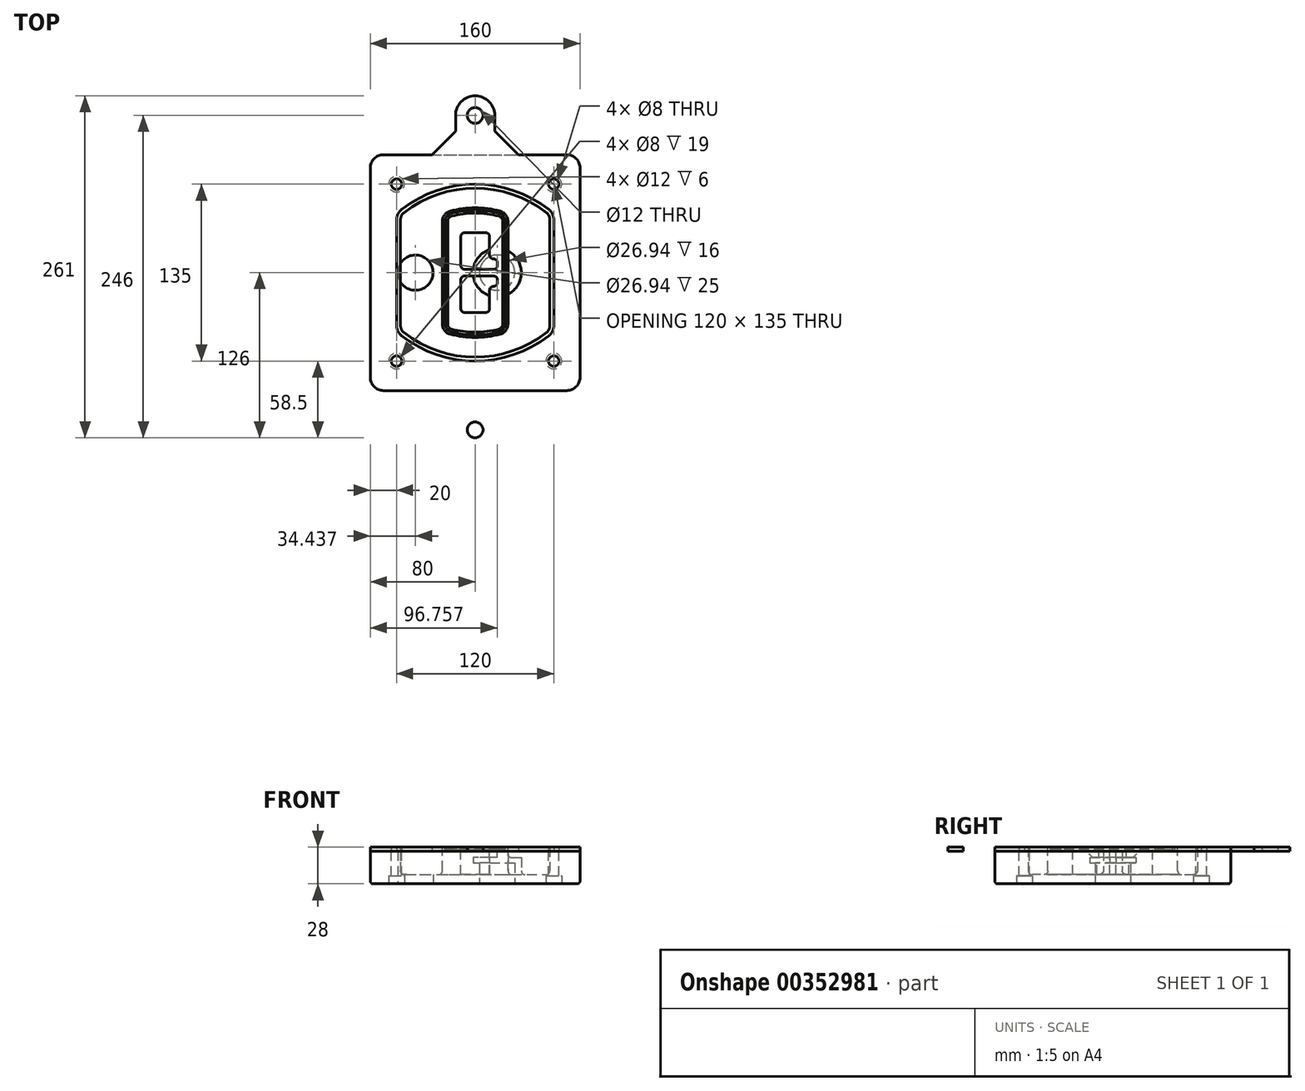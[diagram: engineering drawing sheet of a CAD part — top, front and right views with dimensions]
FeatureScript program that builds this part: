
annotation { "Feature Type Name" : "Feature", "Feature Type Description" : "" }
export const myFeature = defineFeature(function(context is Context, id is Id, definition is map)
    precondition{}
    {
        {
            var Q0;
            Q0=qCreatedBy(makeId("Top.planeOp"),FACE);
            var sketch = newSketch(context, id + "F0", { "sketchPlane" : qUnion([Q0])});
            skPoint(sketch, "E0.rect.middle", {"position": v(0, 0) * mm});
            skLineSegment(sketch, "E1.bottom", {"start": v(-70, -90) * mm, "end": v(70, -90) * mm});
            skLineSegment(sketch, "E1.top", {"start": v(-70, 90) * mm, "end": v(70, 90) * mm});
            skLineSegment(sketch, "E1.left", {"start": v(-80, -80) * mm, "end": v(-80, 80) * mm});
            skLineSegment(sketch, "E1.right", {"start": v(80, -80) * mm, "end": v(80, 80) * mm});
            skLineSegment(sketch, "E2", {"start": v(-80, 90) * mm, "end": v(80, -90) * mm, "construction": true});
            skLineSegment(sketch, "E3", {"start": v(80, 90) * mm, "end": v(-80, -90) * mm, "construction": true});
            skCircle(sketch, "E4", {"center": v(-60, 67.5) * mm, "radius": 4 * mm});
            skCircle(sketch, "E5", {"center": v(60, 67.5) * mm, "radius": 4 * mm});
            skCircle(sketch, "E6", {"center": v(60, -67.5) * mm, "radius": 4 * mm});
            skCircle(sketch, "E7", {"center": v(-60, -67.5) * mm, "radius": 4 * mm});
            skLineSegment(sketch, "E8", {"start": v(-60, 67.5) * mm, "end": v(60, 67.5) * mm, "construction": true});
            skLineSegment(sketch, "E9", {"start": v(60, 67.5) * mm, "end": v(60, -67.5) * mm, "construction": true});
            skLineSegment(sketch, "E10", {"start": v(60, -67.5) * mm, "end": v(-60, -67.5) * mm, "construction": true});
            skLineSegment(sketch, "E11", {"start": v(-60, -67.5) * mm, "end": v(-60, 67.5) * mm, "construction": true});
            skLineSegment(sketch, "E12", {"start": v(-60, 40.3) * mm, "end": v(-60, -40.3) * mm});
            skLineSegment(sketch, "E13", {"start": v(60, 40.3) * mm, "end": v(60, -40.3) * mm});
            skArc(sketch, "E14", {"start": v(56.15, 48.18) * mm, "mid": v(0, 67.5) * mm, "end": v(-56.15, 48.18) * mm});
            skArc(sketch, "E15", {"start": v(-56.15, -48.18) * mm, "mid": v(0, -67.5) * mm, "end": v(56.15, -48.18) * mm});
            skLineSegment(sketch, "E16", {"start": v(-60, 0) * mm, "end": v(60, 0) * mm, "construction": true});
            skPoint(sketch, "E17.visualSharp", {"position": v(-60, -45) * mm});
            skArc(sketch, "E17.filletArc", {"start": v(-60, -40.3) * mm, "mid": v(-58.99, -44.68) * mm, "end": v(-56.15, -48.18) * mm});
            skPoint(sketch, "E18.visualSharp", {"position": v(-60, 45) * mm});
            skArc(sketch, "E18.filletArc", {"start": v(-56.15, 48.18) * mm, "mid": v(-58.99, 44.68) * mm, "end": v(-60, 40.3) * mm});
            skPoint(sketch, "E19.visualSharp", {"position": v(60, 45) * mm});
            skArc(sketch, "E19.filletArc", {"start": v(60, 40.3) * mm, "mid": v(58.99, 44.68) * mm, "end": v(56.15, 48.18) * mm});
            skPoint(sketch, "E20.visualSharp", {"position": v(60, -45) * mm});
            skArc(sketch, "E20.filletArc", {"start": v(56.15, -48.18) * mm, "mid": v(58.99, -44.68) * mm, "end": v(60, -40.3) * mm});
            skPoint(sketch, "E21.visualSharp", {"position": v(-80, 90) * mm});
            skArc(sketch, "E21.filletArc", {"start": v(-70, 90) * mm, "mid": v(-77.07, 87.07) * mm, "end": v(-80, 80) * mm});
            skPoint(sketch, "E22.visualSharp", {"position": v(80, 90) * mm});
            skArc(sketch, "E22.filletArc", {"start": v(80, 80) * mm, "mid": v(77.07, 87.07) * mm, "end": v(70, 90) * mm});
            skPoint(sketch, "E23.visualSharp", {"position": v(80, -90) * mm});
            skArc(sketch, "E23.filletArc", {"start": v(70, -90) * mm, "mid": v(77.07, -87.07) * mm, "end": v(80, -80) * mm});
            skPoint(sketch, "E24.visualSharp", {"position": v(-80, -90) * mm});
            skArc(sketch, "E24.filletArc", {"start": v(-80, -80) * mm, "mid": v(-77.07, -87.07) * mm, "end": v(-70, -90) * mm});
            skArc(sketch, "E25.0", {"start": v(57, 40.3) * mm, "mid": v(56.3, 43.36) * mm, "end": v(54.3, 45.81) * mm});
            skLineSegment(sketch, "E25.1", {"start": v(57, 40.3) * mm, "end": v(57, -40.3) * mm});
            skArc(sketch, "E25.2", {"start": v(54.3, -45.81) * mm, "mid": v(56.3, -43.36) * mm, "end": v(57, -40.3) * mm});
            skArc(sketch, "E25.3", {"start": v(-54.3, -45.81) * mm, "mid": v(0, -64.5) * mm, "end": v(54.3, -45.81) * mm});
            skArc(sketch, "E25.4", {"start": v(-57, -40.3) * mm, "mid": v(-56.3, -43.36) * mm, "end": v(-54.3, -45.81) * mm});
            skArc(sketch, "E25.5", {"start": v(54.3, 45.81) * mm, "mid": v(0, 64.5) * mm, "end": v(-54.3, 45.81) * mm});
            skLineSegment(sketch, "E25.6", {"start": v(-57, 40.3) * mm, "end": v(-57, -40.3) * mm});
            skArc(sketch, "E25.7", {"start": v(-54.3, 45.81) * mm, "mid": v(-56.3, 43.36) * mm, "end": v(-57, 40.3) * mm});
            skArc(sketch, "E26.0", {"start": v(-58.62, 51.33) * mm, "mid": v(-62.58, 46.43) * mm, "end": v(-64, 40.3) * mm});
            skArc(sketch, "E26.1", {"start": v(58.62, 51.33) * mm, "mid": v(0, 71.5) * mm, "end": v(-58.62, 51.33) * mm});
            skArc(sketch, "E26.2", {"start": v(64, 40.3) * mm, "mid": v(62.58, 46.43) * mm, "end": v(58.62, 51.33) * mm});
            skLineSegment(sketch, "E26.3", {"start": v(64, 40.3) * mm, "end": v(64, -40.3) * mm});
            skArc(sketch, "E26.4", {"start": v(58.62, -51.33) * mm, "mid": v(62.58, -46.43) * mm, "end": v(64, -40.3) * mm});
            skLineSegment(sketch, "E26.5", {"start": v(-64, 40.3) * mm, "end": v(-64, -40.3) * mm});
            skArc(sketch, "E26.6", {"start": v(-58.62, -51.33) * mm, "mid": v(0, -71.5) * mm, "end": v(58.62, -51.33) * mm});
            skArc(sketch, "E26.7", {"start": v(-64, -40.3) * mm, "mid": v(-62.58, -46.43) * mm, "end": v(-58.62, -51.33) * mm});
            skSolve(sketch);
        }
        {
            var Q0;
            Q0=makeQuery(id+"F0.imprint","IMPRINT",FACE,{"disambiguationData":[TD([[makeQuery(id+"F0.imprint","IMPRINT",EDGE,{"derivedFrom":sQuery(id+"F0.wireOp",EDGE,"E1.bottom")}),1.0]])]});
            var Q1;
            Q1=makeQuery(id+"F0.imprint","IMPRINT",FACE,{"disambiguationData":[TD([[makeQuery(id+"F0.imprint","IMPRINT",EDGE,{"derivedFrom":sQuery(id+"F0.wireOp",EDGE,"E12")}),1.0]])]});
            var Q2;
            Q2=makeQuery(id+"F0.imprint","IMPRINT",FACE,{"disambiguationData":[TD([[makeQuery(id+"F0.imprint","IMPRINT",EDGE,{"derivedFrom":sQuery(id+"F0.wireOp",EDGE,"E25.0")}),1.0]])]});
            var Q3;
            Q3=makeQuery(id+"F0.imprint","IMPRINT",FACE,{"disambiguationData":[TD([[makeQuery(id+"F0.imprint","IMPRINT",EDGE,{"derivedFrom":sQuery(id+"F0.wireOp",EDGE,"E12")}),-1.0]])]});
            extrude(context, id + "F1", {"entities" : qUnion([Q0, Q1, Q2, Q3]), "oppositeDirection" : true, "depth" : 25 * mm});
        }
        {
            var Q0;
            Q0=makeQuery(id+"F0.imprint","IMPRINT",FACE,{"disambiguationData":[TD([[makeQuery(id+"F0.imprint","IMPRINT",EDGE,{"derivedFrom":sQuery(id+"F0.wireOp",EDGE,"E12")}),1.0]])]});
            extrude(context, id + "F2", {"entities" : qUnion([Q0]), "operationType" : NewBodyOperationType.ADD, "depth" : 3 * mm});
        }
        {
            var Q0;
            Q0=makeQuery(id+"F0.imprint","IMPRINT",FACE,{"disambiguationData":[TD([[makeQuery(id+"F0.imprint","IMPRINT",EDGE,{"derivedFrom":sQuery(id+"F0.wireOp",EDGE,"E25.0")}),1.0]])]});
            extrude(context, id + "F3", {"entities" : qUnion([Q0]), "operationType" : NewBodyOperationType.REMOVE, "oppositeDirection" : true, "depth" : 18 * mm});
        }
        {
            var Q0;
            Q0=makeQuery(id+"F2.opExtrude","CAP_FACE",FACE,{"disambiguationData":[OSD([sQuery(id+"F0.wireOp",EDGE,"E12"),sQuery(id+"F0.wireOp",EDGE,"E13"),sQuery(id+"F0.wireOp",EDGE,"E14"),sQuery(id+"F0.wireOp",EDGE,"E15"),sQuery(id+"F0.wireOp",EDGE,"E17.filletArc"),sQuery(id+"F0.wireOp",EDGE,"E18.filletArc"),sQuery(id+"F0.wireOp",EDGE,"E19.filletArc"),sQuery(id+"F0.wireOp",EDGE,"E20.filletArc"),sQuery(id+"F0.wireOp",EDGE,"E25.0"),sQuery(id+"F0.wireOp",EDGE,"E25.1"),sQuery(id+"F0.wireOp",EDGE,"E25.2"),sQuery(id+"F0.wireOp",EDGE,"E25.3"),sQuery(id+"F0.wireOp",EDGE,"E25.4"),sQuery(id+"F0.wireOp",EDGE,"E25.5"),sQuery(id+"F0.wireOp",EDGE,"E25.6"),sQuery(id+"F0.wireOp",EDGE,"E25.7")])],"isStart":false});
            var sketch = newSketch(context, id + "F4", { "sketchPlane" : qUnion([Q0])});
            skArc(sketch, "E27.0", {"start": v(-19.08, -46.97) * mm, "mid": v(0, -49.5) * mm, "end": v(19.08, -46.97) * mm});
            skArc(sketch, "E28.0", {"start": v(19.08, 46.97) * mm, "mid": v(0, 49.5) * mm, "end": v(-19.08, 46.97) * mm});
            skLineSegment(sketch, "E29", {"start": v(-25, 39.25) * mm, "end": v(-25, -39.25) * mm});
            skLineSegment(sketch, "E30", {"start": v(25, 39.25) * mm, "end": v(25, -39.25) * mm});
            skLineSegment(sketch, "E31", {"start": v(-25, 45.1) * mm, "end": v(25, 45.1) * mm, "construction": true});
            skLineSegment(sketch, "E32", {"start": v(-25, -45.1) * mm, "end": v(25, -45.1) * mm, "construction": true});
            skPoint(sketch, "E33.visualSharp", {"position": v(-25, 45.1) * mm});
            skArc(sketch, "E33.filletArc", {"start": v(-19.08, 46.97) * mm, "mid": v(-23.35, 44.11) * mm, "end": v(-25, 39.25) * mm});
            skPoint(sketch, "E34.visualSharp", {"position": v(25, 45.1) * mm});
            skArc(sketch, "E34.filletArc", {"start": v(25, 39.25) * mm, "mid": v(23.35, 44.11) * mm, "end": v(19.08, 46.97) * mm});
            skPoint(sketch, "E35.visualSharp", {"position": v(25, -45.1) * mm});
            skArc(sketch, "E35.filletArc", {"start": v(19.08, -46.97) * mm, "mid": v(23.35, -44.11) * mm, "end": v(25, -39.25) * mm});
            skPoint(sketch, "E36.visualSharp", {"position": v(-25, -45.1) * mm});
            skArc(sketch, "E36.filletArc", {"start": v(-25, -39.25) * mm, "mid": v(-23.35, -44.11) * mm, "end": v(-19.08, -46.97) * mm});
            skArc(sketch, "E37.0", {"start": v(54.3, 45.81) * mm, "mid": v(0, 64.5) * mm, "end": v(-54.3, 45.81) * mm});
            skArc(sketch, "E37.1", {"start": v(-54.3, 45.81) * mm, "mid": v(-56.3, 43.36) * mm, "end": v(-57, 40.3) * mm});
            skLineSegment(sketch, "E37.2", {"start": v(-57, 40.3) * mm, "end": v(-57, -40.3) * mm});
            skArc(sketch, "E37.3", {"start": v(-57, -40.3) * mm, "mid": v(-56.3, -43.36) * mm, "end": v(-54.3, -45.81) * mm});
            skArc(sketch, "E37.4", {"start": v(-54.3, -45.81) * mm, "mid": v(0, -64.5) * mm, "end": v(54.3, -45.81) * mm});
            skArc(sketch, "E37.5", {"start": v(54.3, -45.81) * mm, "mid": v(56.3, -43.36) * mm, "end": v(57, -40.3) * mm});
            skLineSegment(sketch, "E37.6", {"start": v(57, 40.3) * mm, "end": v(57, -40.3) * mm});
            skArc(sketch, "E37.7", {"start": v(57, 40.3) * mm, "mid": v(56.3, 43.36) * mm, "end": v(54.3, 45.81) * mm});
            skLineSegment(sketch, "E38.0", {"start": v(23, 39.25) * mm, "end": v(23, -39.25) * mm});
            skArc(sketch, "E38.1", {"start": v(18.56, -45.04) * mm, "mid": v(21.76, -42.9) * mm, "end": v(23, -39.25) * mm});
            skArc(sketch, "E38.2", {"start": v(-18.56, -45.04) * mm, "mid": v(0, -47.5) * mm, "end": v(18.56, -45.04) * mm});
            skArc(sketch, "E38.3", {"start": v(-23, -39.25) * mm, "mid": v(-21.76, -42.9) * mm, "end": v(-18.56, -45.04) * mm});
            skLineSegment(sketch, "E38.4", {"start": v(-23, 39.25) * mm, "end": v(-23, -39.25) * mm});
            skArc(sketch, "E38.5", {"start": v(23, 39.25) * mm, "mid": v(21.76, 42.9) * mm, "end": v(18.56, 45.04) * mm});
            skArc(sketch, "E38.6", {"start": v(-18.56, 45.04) * mm, "mid": v(-21.76, 42.9) * mm, "end": v(-23, 39.25) * mm});
            skArc(sketch, "E38.7", {"start": v(18.56, 45.04) * mm, "mid": v(0, 47.5) * mm, "end": v(-18.56, 45.04) * mm});
            skArc(sketch, "E39.0", {"start": v(21, 39.25) * mm, "mid": v(20.18, 41.68) * mm, "end": v(18.04, 43.1) * mm});
            skLineSegment(sketch, "E39.1", {"start": v(21, 39.25) * mm, "end": v(21, -39.25) * mm});
            skArc(sketch, "E39.2", {"start": v(18.04, -43.1) * mm, "mid": v(20.18, -41.68) * mm, "end": v(21, -39.25) * mm});
            skArc(sketch, "E39.3", {"start": v(-18.04, -43.1) * mm, "mid": v(0, -45.5) * mm, "end": v(18.04, -43.1) * mm});
            skArc(sketch, "E39.4", {"start": v(-21, -39.25) * mm, "mid": v(-20.18, -41.68) * mm, "end": v(-18.04, -43.1) * mm});
            skArc(sketch, "E39.5", {"start": v(18.04, 43.1) * mm, "mid": v(0, 45.5) * mm, "end": v(-18.04, 43.1) * mm});
            skLineSegment(sketch, "E39.6", {"start": v(-21, 39.25) * mm, "end": v(-21, -39.25) * mm});
            skArc(sketch, "E39.7", {"start": v(-18.04, 43.1) * mm, "mid": v(-20.18, 41.68) * mm, "end": v(-21, 39.25) * mm});
            skLineSegment(sketch, "E40", {"start": v(-25, 0) * mm, "end": v(25, 0) * mm, "construction": true});
            skLineSegment(sketch, "E41", {"start": v(-11, 5.5) * mm, "end": v(-11, 27.5) * mm});
            skLineSegment(sketch, "E42", {"start": v(-8, 30.5) * mm, "end": v(8, 30.5) * mm});
            skLineSegment(sketch, "E43", {"start": v(11, 27.5) * mm, "end": v(11, 13.5) * mm});
            skLineSegment(sketch, "E44", {"start": v(14, 10.5) * mm, "end": v(14, 10.5) * mm});
            skLineSegment(sketch, "E45", {"start": v(17, 7.5) * mm, "end": v(17, 5.5) * mm});
            skLineSegment(sketch, "E46", {"start": v(14, 2.5) * mm, "end": v(-8, 2.5) * mm});
            skPoint(sketch, "E47.visualSharp", {"position": v(-11, 30.5) * mm});
            skArc(sketch, "E47.filletArc", {"start": v(-8, 30.5) * mm, "mid": v(-10.12, 29.62) * mm, "end": v(-11, 27.5) * mm});
            skPoint(sketch, "E48.visualSharp", {"position": v(11, 30.5) * mm});
            skArc(sketch, "E48.filletArc", {"start": v(11, 27.5) * mm, "mid": v(10.12, 29.62) * mm, "end": v(8, 30.5) * mm});
            skPoint(sketch, "E49.visualSharp", {"position": v(11, 10.5) * mm});
            skArc(sketch, "E49.filletArc", {"start": v(11, 13.5) * mm, "mid": v(11.88, 11.38) * mm, "end": v(14, 10.5) * mm});
            skPoint(sketch, "E50.visualSharp", {"position": v(17, 10.5) * mm});
            skArc(sketch, "E50.filletArc", {"start": v(17, 7.5) * mm, "mid": v(16.12, 9.62) * mm, "end": v(14, 10.5) * mm});
            skPoint(sketch, "E51.visualSharp", {"position": v(17, 2.5) * mm});
            skArc(sketch, "E51.filletArc", {"start": v(14, 2.5) * mm, "mid": v(16.12, 3.38) * mm, "end": v(17, 5.5) * mm});
            skPoint(sketch, "E52.visualSharp", {"position": v(-11, 2.5) * mm});
            skArc(sketch, "E52.filletArc", {"start": v(-11, 5.5) * mm, "mid": v(-10.12, 3.38) * mm, "end": v(-8, 2.5) * mm});
            skLineSegment(sketch, "E53.0.MirrorCS", {"start": v(14, -2.5) * mm, "end": v(-8, -2.5) * mm});
            skArc(sketch, "E54.0.MirrorCS", {"start": v(-11, -5.5) * mm, "mid": v(-10.12, -3.38) * mm, "end": v(-8, -2.5) * mm});
            skLineSegment(sketch, "E55.0.MirrorCS", {"start": v(-11, -5.5) * mm, "end": v(-11, -27.5) * mm});
            skArc(sketch, "E56.0.MirrorCS", {"start": v(-8, -30.5) * mm, "mid": v(-10.12, -29.62) * mm, "end": v(-11, -27.5) * mm});
            skLineSegment(sketch, "E57.0.MirrorCS", {"start": v(-8, -30.5) * mm, "end": v(8, -30.5) * mm});
            skArc(sketch, "E58.0.MirrorCS", {"start": v(11, -27.5) * mm, "mid": v(10.12, -29.62) * mm, "end": v(8, -30.5) * mm});
            skLineSegment(sketch, "E59.0.MirrorCS", {"start": v(11, -27.5) * mm, "end": v(11, -13.5) * mm});
            skArc(sketch, "E60.0.MirrorCS", {"start": v(11, -13.5) * mm, "mid": v(11.88, -11.38) * mm, "end": v(14, -10.5) * mm});
            skArc(sketch, "E61.0.MirrorCS", {"start": v(17, -7.5) * mm, "mid": v(16.12, -9.62) * mm, "end": v(14, -10.5) * mm});
            skLineSegment(sketch, "E62.0.MirrorCS", {"start": v(17, -7.5) * mm, "end": v(17, -5.5) * mm});
            skArc(sketch, "E63.0.MirrorCS", {"start": v(14, -2.5) * mm, "mid": v(16.12, -3.38) * mm, "end": v(17, -5.5) * mm});
            skSolve(sketch);
        }
        {
            var Q0;
            Q0=makeQuery(id+"F4.imprint","IMPRINT",FACE,{"disambiguationData":[TD([[makeQuery(id+"F4.imprint","IMPRINT",EDGE,{"derivedFrom":sQuery(id+"F4.wireOp",EDGE,"E27.0")}),1.0]])]});
            var Q1;
            Q1=makeQuery(id+"F4.imprint","IMPRINT",FACE,{"disambiguationData":[TD([[makeQuery(id+"F4.imprint","IMPRINT",EDGE,{"derivedFrom":sQuery(id+"F4.wireOp",EDGE,"E38.0")}),-1.0]])]});
            var Q2;
            Q2=makeQuery(id+"F4.imprint","IMPRINT",FACE,{"disambiguationData":[TD([[makeQuery(id+"F4.imprint","IMPRINT",EDGE,{"derivedFrom":sQuery(id+"F4.wireOp",EDGE,"E39.0")}),1.0]])]});
            extrude(context, id + "F5", {"entities" : qUnion([Q0, Q1, Q2]), "operationType" : NewBodyOperationType.ADD, "endBound" : BoundingType.UP_TO_NEXT, "oppositeDirection" : true, "depth" : 25 * mm});
        }
        {
            var Q0;
            Q0=makeQuery(id+"F4.imprint","IMPRINT",FACE,{"disambiguationData":[TD([[makeQuery(id+"F4.imprint","IMPRINT",EDGE,{"derivedFrom":sQuery(id+"F4.wireOp",EDGE,"E38.0")}),-1.0]])]});
            extrude(context, id + "F6", {"entities" : qUnion([Q0]), "operationType" : NewBodyOperationType.REMOVE, "oppositeDirection" : true, "depth" : 2 * mm});
        }
        {
            var Q0;
            Q0=makeQuery(id+"F1.opExtrude","CAP_FACE",FACE,{"disambiguationData":[OSD([sQuery(id+"F0.wireOp",EDGE,"E1.bottom"),sQuery(id+"F0.wireOp",EDGE,"E1.top"),sQuery(id+"F0.wireOp",EDGE,"E1.left"),sQuery(id+"F0.wireOp",EDGE,"E1.right"),sQuery(id+"F0.wireOp",EDGE,"E4"),sQuery(id+"F0.wireOp",EDGE,"E5"),sQuery(id+"F0.wireOp",EDGE,"E6"),sQuery(id+"F0.wireOp",EDGE,"E7"),sQuery(id+"F0.wireOp",EDGE,"E21.filletArc"),sQuery(id+"F0.wireOp",EDGE,"E22.filletArc"),sQuery(id+"F0.wireOp",EDGE,"E23.filletArc"),sQuery(id+"F0.wireOp",EDGE,"E24.filletArc")])],"isStart":false});
            var sketch = newSketch(context, id + "F7", { "sketchPlane" : qUnion([Q0])});
            skCircle(sketch, "E64", {"center": v(16.76, 0) * mm, "radius": 13.47 * mm});
            skCircle(sketch, "E65", {"center": v(-45.56, 0) * mm, "radius": 13.47 * mm});
            skLineSegment(sketch, "E66", {"start": v(80, 0) * mm, "end": v(-80, 0) * mm});
            skCircle(sketch, "E67", {"center": v(16.76, 0) * mm, "radius": 18.47 * mm});
            skCircle(sketch, "E68", {"center": v(60, -67.5) * mm, "radius": 6 * mm});
            skCircle(sketch, "E69", {"center": v(-60, -67.5) * mm, "radius": 6 * mm});
            skCircle(sketch, "E70", {"center": v(-60, 67.5) * mm, "radius": 6 * mm});
            skCircle(sketch, "E71", {"center": v(60, 67.5) * mm, "radius": 6 * mm});
            skSolve(sketch);
        }
        {
            var Q0;
            {var subQ1=sQuery(id+"F7.wireOp",EDGE,"E66");var subQ4=sQuery(id+"F7.wireOp",EDGE,"E64");var subQ6=makeQuery(id+"F7.imprint","INTERSECT",VERTEX,{"disambiguationData":[OD(0.0)],"derivedFrom":[subQ4,subQ1]});Q0=makeQuery(id+"F7.imprint","IMPRINT",FACE,{"disambiguationData":[TD([[makeQuery(id+"F7.imprint","IMPRINT",EDGE,{"disambiguationData":[TD([[subQ6,-1.0]])],"derivedFrom":subQ4}),-1.0]])]});}
            var Q1;
            {var subQ0=sQuery(id+"F7.wireOp",EDGE,"E66");var subQ1=sQuery(id+"F7.wireOp",EDGE,"E64");var subQ3=makeQuery(id+"F7.imprint","INTERSECT",VERTEX,{"disambiguationData":[OD(0.0)],"derivedFrom":[subQ1,subQ0]});Q1=makeQuery(id+"F7.imprint","IMPRINT",FACE,{"disambiguationData":[TD([[makeQuery(id+"F7.imprint","IMPRINT",EDGE,{"disambiguationData":[TD([[subQ3,-1.0]])],"derivedFrom":subQ1}),1.0]])]});}
            var Q2;
            {var subQ0=sQuery(id+"F7.wireOp",EDGE,"E66");var subQ1=sQuery(id+"F7.wireOp",EDGE,"E64");var subQ3=makeQuery(id+"F7.imprint","INTERSECT",VERTEX,{"disambiguationData":[OD(0.0)],"derivedFrom":[subQ1,subQ0]});Q2=makeQuery(id+"F7.imprint","IMPRINT",FACE,{"disambiguationData":[TD([[makeQuery(id+"F7.imprint","IMPRINT",EDGE,{"disambiguationData":[TD([[subQ3,1.0]])],"derivedFrom":subQ1}),1.0]])]});}
            var Q3;
            {var subQ1=sQuery(id+"F7.wireOp",EDGE,"E66");var subQ4=sQuery(id+"F7.wireOp",EDGE,"E64");var subQ6=makeQuery(id+"F7.imprint","INTERSECT",VERTEX,{"disambiguationData":[OD(0.0)],"derivedFrom":[subQ4,subQ1]});Q3=makeQuery(id+"F7.imprint","IMPRINT",FACE,{"disambiguationData":[TD([[makeQuery(id+"F7.imprint","IMPRINT",EDGE,{"disambiguationData":[TD([[subQ6,1.0]])],"derivedFrom":subQ4}),-1.0]])]});}
            extrude(context, id + "F8", {"entities" : qUnion([Q0, Q1, Q2, Q3]), "operationType" : NewBodyOperationType.ADD, "oppositeDirection" : true, "depth" : 20 * mm});
        }
        {
            var Q0;
            {var subQ0=sQuery(id+"F7.wireOp",EDGE,"E66");var subQ1=sQuery(id+"F7.wireOp",EDGE,"E64");var subQ3=makeQuery(id+"F7.imprint","INTERSECT",VERTEX,{"disambiguationData":[OD(0.0)],"derivedFrom":[subQ1,subQ0]});Q0=makeQuery(id+"F7.imprint","IMPRINT",FACE,{"disambiguationData":[TD([[makeQuery(id+"F7.imprint","IMPRINT",EDGE,{"disambiguationData":[TD([[subQ3,-1.0]])],"derivedFrom":subQ1}),1.0]])]});}
            var Q1;
            {var subQ0=sQuery(id+"F7.wireOp",EDGE,"E66");var subQ1=sQuery(id+"F7.wireOp",EDGE,"E64");var subQ3=makeQuery(id+"F7.imprint","INTERSECT",VERTEX,{"disambiguationData":[OD(0.0)],"derivedFrom":[subQ1,subQ0]});Q1=makeQuery(id+"F7.imprint","IMPRINT",FACE,{"disambiguationData":[TD([[makeQuery(id+"F7.imprint","IMPRINT",EDGE,{"disambiguationData":[TD([[subQ3,1.0]])],"derivedFrom":subQ1}),1.0]])]});}
            extrude(context, id + "F9", {"entities" : qUnion([Q0, Q1]), "operationType" : NewBodyOperationType.REMOVE, "oppositeDirection" : true, "depth" : 16 * mm});
        }
        {
            var Q0;
            {var subQ0=sQuery(id+"F7.wireOp",EDGE,"E66");var subQ1=sQuery(id+"F7.wireOp",EDGE,"E65");var subQ3=makeQuery(id+"F7.imprint","INTERSECT",VERTEX,{"disambiguationData":[OD(0.0)],"derivedFrom":[subQ1,subQ0]});Q0=makeQuery(id+"F7.imprint","IMPRINT",FACE,{"disambiguationData":[TD([[makeQuery(id+"F7.imprint","IMPRINT",EDGE,{"disambiguationData":[TD([[subQ3,-1.0]])],"derivedFrom":subQ1}),1.0]])]});}
            var Q1;
            {var subQ0=sQuery(id+"F7.wireOp",EDGE,"E66");var subQ1=sQuery(id+"F7.wireOp",EDGE,"E65");var subQ3=makeQuery(id+"F7.imprint","INTERSECT",VERTEX,{"disambiguationData":[OD(0.0)],"derivedFrom":[subQ1,subQ0]});Q1=makeQuery(id+"F7.imprint","IMPRINT",FACE,{"disambiguationData":[TD([[makeQuery(id+"F7.imprint","IMPRINT",EDGE,{"disambiguationData":[TD([[subQ3,1.0]])],"derivedFrom":subQ1}),1.0]])]});}
            extrude(context, id + "F10", {"entities" : qUnion([Q0, Q1]), "operationType" : NewBodyOperationType.REMOVE, "oppositeDirection" : true, "depth" : 25 * mm});
        }
        {
            var Q0;
            Q0=makeQuery(id+"F7.imprint","IMPRINT",FACE,{"disambiguationData":[TD([[makeQuery(id+"F7.imprint","IMPRINT",EDGE,{"derivedFrom":sQuery(id+"F7.wireOp",EDGE,"E68")}),1.0]])]});
            var Q1;
            Q1=makeQuery(id+"F7.imprint","IMPRINT",FACE,{"disambiguationData":[TD([[makeQuery(id+"F7.imprint","IMPRINT",EDGE,{"derivedFrom":makeQuery(id+"F1.opExtrude","CAP_EDGE",EDGE,{"disambiguationData":[OSD([sQuery(id+"F0.wireOp",EDGE,"E5")])],"isStart":false})}),-1.0]])]});
            var Q2;
            Q2=makeQuery(id+"F7.imprint","IMPRINT",FACE,{"disambiguationData":[TD([[makeQuery(id+"F7.imprint","IMPRINT",EDGE,{"derivedFrom":sQuery(id+"F7.wireOp",EDGE,"E69")}),1.0]])]});
            var Q3;
            Q3=makeQuery(id+"F7.imprint","IMPRINT",FACE,{"disambiguationData":[TD([[makeQuery(id+"F7.imprint","IMPRINT",EDGE,{"derivedFrom":makeQuery(id+"F1.opExtrude","CAP_EDGE",EDGE,{"disambiguationData":[OSD([sQuery(id+"F0.wireOp",EDGE,"E4")])],"isStart":false})}),-1.0]])]});
            var Q4;
            Q4=makeQuery(id+"F7.imprint","IMPRINT",FACE,{"disambiguationData":[TD([[makeQuery(id+"F7.imprint","IMPRINT",EDGE,{"derivedFrom":sQuery(id+"F7.wireOp",EDGE,"E70")}),1.0]])]});
            var Q5;
            Q5=makeQuery(id+"F7.imprint","IMPRINT",FACE,{"disambiguationData":[TD([[makeQuery(id+"F7.imprint","IMPRINT",EDGE,{"derivedFrom":makeQuery(id+"F1.opExtrude","CAP_EDGE",EDGE,{"disambiguationData":[OSD([sQuery(id+"F0.wireOp",EDGE,"E7")])],"isStart":false})}),-1.0]])]});
            var Q6;
            Q6=makeQuery(id+"F7.imprint","IMPRINT",FACE,{"disambiguationData":[TD([[makeQuery(id+"F7.imprint","IMPRINT",EDGE,{"derivedFrom":sQuery(id+"F7.wireOp",EDGE,"E71")}),1.0]])]});
            var Q7;
            Q7=makeQuery(id+"F7.imprint","IMPRINT",FACE,{"disambiguationData":[TD([[makeQuery(id+"F7.imprint","IMPRINT",EDGE,{"derivedFrom":makeQuery(id+"F1.opExtrude","CAP_EDGE",EDGE,{"disambiguationData":[OSD([sQuery(id+"F0.wireOp",EDGE,"E6")])],"isStart":false})}),-1.0]])]});
            extrude(context, id + "F11", {"entities" : qUnion([Q0, Q1, Q2, Q3, Q4, Q5, Q6, Q7]), "operationType" : NewBodyOperationType.REMOVE, "oppositeDirection" : true, "depth" : 6 * mm});
        }
        {
            var Q0;
            Q0=makeQuery(id+"F9.boolean.opBoolean","COPY",FACE,{"derivedFrom":makeQuery(id+"F9.opExtrude","CAP_FACE",FACE,{"disambiguationData":[OSD([sQuery(id+"F7.wireOp",EDGE,"E64")])],"isStart":false})});
            var sketch = newSketch(context, id + "F12", { "sketchPlane" : qUnion([Q0])});
            skArc(sketch, "E72.0", {"start": v(11, 17.55) * mm, "mid": v(2.57, 11.82) * mm, "end": v(-1.54, 2.5) * mm});
            skArc(sketch, "E72.1", {"start": v(-1.54, -2.5) * mm, "mid": v(2.57, -11.82) * mm, "end": v(11, -17.55) * mm});
            skLineSegment(sketch, "E73", {"start": v(-1.54, -2.5) * mm, "end": v(14, -2.5) * mm});
            skLineSegment(sketch, "E74.0", {"start": v(14, 2.5) * mm, "end": v(-1.54, 2.5) * mm});
            skArc(sketch, "E74.1", {"start": v(14, 2.5) * mm, "mid": v(16.12, 3.38) * mm, "end": v(17, 5.5) * mm});
            skLineSegment(sketch, "E74.2", {"start": v(17, 7.5) * mm, "end": v(17, 5.5) * mm});
            skArc(sketch, "E74.3", {"start": v(17, 7.5) * mm, "mid": v(16.12, 9.62) * mm, "end": v(14, 10.5) * mm});
            skArc(sketch, "E74.4", {"start": v(11, 13.5) * mm, "mid": v(11.88, 11.38) * mm, "end": v(14, 10.5) * mm});
            skLineSegment(sketch, "E74.5", {"start": v(11, 17.55) * mm, "end": v(11, 13.5) * mm});
            skLineSegment(sketch, "E74.7", {"start": v(14, -2.5) * mm, "end": v(-1.54, -2.5) * mm});
            skArc(sketch, "E74.8", {"start": v(14, -2.5) * mm, "mid": v(16.12, -3.38) * mm, "end": v(17, -5.5) * mm});
            skLineSegment(sketch, "E74.9", {"start": v(17, -7.5) * mm, "end": v(17, -5.5) * mm});
            skArc(sketch, "E74.10", {"start": v(17, -7.5) * mm, "mid": v(16.12, -9.62) * mm, "end": v(14, -10.5) * mm});
            skArc(sketch, "E74.11", {"start": v(11, -13.5) * mm, "mid": v(11.88, -11.38) * mm, "end": v(14, -10.5) * mm});
            skLineSegment(sketch, "E74.12", {"start": v(11, -17.55) * mm, "end": v(11, -13.5) * mm});
            skPoint(sketch, "E75.orphan", {"position": v(11, -27.5) * mm});
            skPoint(sketch, "E76.orphan", {"position": v(-8, -2.5) * mm});
            skPoint(sketch, "E77.orphan", {"position": v(-8, 2.5) * mm});
            skPoint(sketch, "E78.orphan", {"position": v(11, 27.5) * mm});
            skSolve(sketch);
        }
        {
            var Q0;
            {var subQ7=sQuery(id+"F12.wireOp",EDGE,"E72.0");var subQ14=sQuery(id+"F12.wireOp",EDGE,"E72.1");var subQ16=sQuery(id+"F12.wireOp",EDGE,"E74.1");var subQ18=sQuery(id+"F12.wireOp",EDGE,"E74.8");Q0=qUnion([makeQuery(id+"F12.imprint","IMPRINT",FACE,{"disambiguationData":[TD([[makeQuery(id+"F12.imprint","IMPRINT",EDGE,{"derivedFrom":subQ7}),1.0]])]}),makeQuery(id+"F12.imprint","IMPRINT",FACE,{"disambiguationData":[TD([[makeQuery(id+"F12.imprint","IMPRINT",EDGE,{"derivedFrom":subQ14}),1.0]])]}),makeQuery(id+"F12.imprint","IMPRINT",FACE,{"disambiguationData":[TD([[makeQuery(id+"F12.imprint","IMPRINT",EDGE,{"derivedFrom":subQ16}),1.0]])]}),makeQuery(id+"F12.imprint","IMPRINT",FACE,{"disambiguationData":[TD([[makeQuery(id+"F12.imprint","IMPRINT",EDGE,{"derivedFrom":subQ18}),-1.0]])]})]);}
            var Q1;
            Q1=makeQuery(id+"F5.boolean.opBoolean","SPLIT",FACE,{"disambiguationData":[TD([makeQuery(id+"F5.opExtrude","SWEPT_FACE",FACE,{"disambiguationData":[OSD([sQuery(id+"F4.wireOp",EDGE,"E41")])]})])],"derivedFrom":makeQuery(id+"F3.boolean.opBoolean","COPY",FACE,{"derivedFrom":makeQuery(id+"F3.opExtrude","CAP_FACE",FACE,{"disambiguationData":[OSD([sQuery(id+"F0.wireOp",EDGE,"E25.0"),sQuery(id+"F0.wireOp",EDGE,"E25.1"),sQuery(id+"F0.wireOp",EDGE,"E25.2"),sQuery(id+"F0.wireOp",EDGE,"E25.3"),sQuery(id+"F0.wireOp",EDGE,"E25.4"),sQuery(id+"F0.wireOp",EDGE,"E25.5"),sQuery(id+"F0.wireOp",EDGE,"E25.6"),sQuery(id+"F0.wireOp",EDGE,"E25.7")])],"isStart":false})})});
            extrude(context, id + "F13", {"entities" : qUnion([Q0]), "operationType" : NewBodyOperationType.REMOVE, "endBound" : BoundingType.UP_TO_SURFACE, "endBoundEntityFace" : qUnion([Q1]), "depth" : 25 * mm});
        }
        {
            var Q0;
            Q0=makeQuery(id+"F3.boolean.opBoolean","COPY",EDGE,{"derivedFrom":makeQuery(id+"F3.opExtrude","CAP_EDGE",EDGE,{"disambiguationData":[OSD([sQuery(id+"F0.wireOp",EDGE,"E25.6")])],"isStart":false})});
            var Q1;
            Q1=makeQuery(id+"F8.boolean.opBoolean","INTERSECT",EDGE,{"derivedFrom":[makeQuery(id+"F5.opExtrude","SWEPT_FACE",FACE,{"disambiguationData":[OSD([sQuery(id+"F4.wireOp",EDGE,"E30")])]}),makeQuery(id+"F8.opExtrude","CAP_FACE",FACE,{"disambiguationData":[OSD([sQuery(id+"F7.wireOp",EDGE,"E67")])],"isStart":false})]});
            var Q2;
            Q2=makeQuery(id+"F8.boolean.opBoolean","INTERSECT",EDGE,{"disambiguationData":[OD(1.0)],"derivedFrom":[makeQuery(id+"F5.opExtrude","SWEPT_FACE",FACE,{"disambiguationData":[OSD([sQuery(id+"F4.wireOp",EDGE,"E30")])]}),makeQuery(id+"F8.opExtrude","SWEPT_FACE",FACE,{"disambiguationData":[OSD([sQuery(id+"F7.wireOp",EDGE,"E67")])]})]});
            var Q3;
            {var subQ0=sQuery(id+"F4.wireOp",EDGE,"E30");Q3=makeQuery(id+"F8.boolean.opBoolean","SPLIT",EDGE,{"disambiguationData":[TD([makeQuery(id+"F5.opExtrude","SWEPT_FACE",FACE,{"disambiguationData":[OSD([sQuery(id+"F4.wireOp",EDGE,"E35.filletArc")])]})])],"derivedFrom":makeQuery(id+"F5.opExtrude","CAP_EDGE",EDGE,{"disambiguationData":[OSD([subQ0])],"isStart":false})});}
            var Q4;
            {var subQ0=sQuery(id+"F0.wireOp",EDGE,"E25.7");var subQ1=sQuery(id+"F0.wireOp",EDGE,"E25.1");var subQ2=sQuery(id+"F0.wireOp",EDGE,"E25.6");var subQ3=sQuery(id+"F0.wireOp",EDGE,"E25.5");var subQ4=sQuery(id+"F0.wireOp",EDGE,"E25.4");var subQ5=sQuery(id+"F0.wireOp",EDGE,"E25.0");var subQ6=sQuery(id+"F0.wireOp",EDGE,"E25.2");var subQ7=sQuery(id+"F0.wireOp",EDGE,"E25.3");Q4=makeQuery(id+"F8.boolean.opBoolean","INTERSECT",EDGE,{"derivedFrom":[makeQuery(id+"F5.boolean.opBoolean","SPLIT",FACE,{"disambiguationData":[TD([makeQuery(id+"F2.opExtrude","SWEPT_FACE",FACE,{"disambiguationData":[OSD([subQ5])]})])],"derivedFrom":makeQuery(id+"F3.boolean.opBoolean","COPY",FACE,{"derivedFrom":makeQuery(id+"F3.opExtrude","CAP_FACE",FACE,{"disambiguationData":[OSD([subQ5,subQ1,subQ6,subQ7,subQ4,subQ3,subQ2,subQ0])],"isStart":false})})}),makeQuery(id+"F8.opExtrude","SWEPT_FACE",FACE,{"disambiguationData":[OSD([sQuery(id+"F7.wireOp",EDGE,"E67")])]})]});}
            var Q5;
            Q5=makeQuery(id+"F8.boolean.opBoolean","INTERSECT",EDGE,{"disambiguationData":[OD(0.0)],"derivedFrom":[makeQuery(id+"F5.opExtrude","SWEPT_FACE",FACE,{"disambiguationData":[OSD([sQuery(id+"F4.wireOp",EDGE,"E30")])]}),makeQuery(id+"F8.opExtrude","SWEPT_FACE",FACE,{"disambiguationData":[OSD([sQuery(id+"F7.wireOp",EDGE,"E67")])]})]});
            fillet(context, id + "F14", {"entities" : qUnion([Q0, Q1, Q2, Q3, Q4, Q5]), "radius" : 3 * mm, "tangentPropagation" : true, "allowEdgeOverflow" : false});
        }
        {
            var Q0;
            Q0=makeQuery(id+"F1.opExtrude","CAP_EDGE",EDGE,{"disambiguationData":[OSD([sQuery(id+"F0.wireOp",EDGE,"E1.bottom")])],"isStart":false});
            fillet(context, id + "F15", {"entities" : qUnion([Q0]), "radius" : 2 * mm, "tangentPropagation" : true, "allowEdgeOverflow" : false});
        }
        {
            var Q0;
            {var subQ0=sQuery(id+"F0.wireOp",EDGE,"E21.filletArc");var subQ1=sQuery(id+"F0.wireOp",EDGE,"E7");var subQ2=sQuery(id+"F0.wireOp",EDGE,"E6");var subQ3=sQuery(id+"F0.wireOp",EDGE,"E5");var subQ4=sQuery(id+"F0.wireOp",EDGE,"E4");var subQ5=sQuery(id+"F0.wireOp",EDGE,"E22.filletArc");var subQ6=sQuery(id+"F0.wireOp",EDGE,"E1.bottom");var subQ7=sQuery(id+"F0.wireOp",EDGE,"E1.right");var subQ8=sQuery(id+"F0.wireOp",EDGE,"E1.top");var subQ9=sQuery(id+"F0.wireOp",EDGE,"E1.left");var subQ10=sQuery(id+"F0.wireOp",EDGE,"E23.filletArc");var subQ11=sQuery(id+"F0.wireOp",EDGE,"E24.filletArc");Q0=makeQuery(id+"F2.boolean.opBoolean","SPLIT",FACE,{"disambiguationData":[TD([makeQuery(id+"F1.opExtrude","SWEPT_FACE",FACE,{"disambiguationData":[OSD([subQ6])]})])],"derivedFrom":makeQuery(id+"F1.opExtrude","CAP_FACE",FACE,{"disambiguationData":[OSD([subQ6,subQ8,subQ9,subQ7,subQ4,subQ3,subQ2,subQ1,subQ0,subQ5,subQ10,subQ11])],"isStart":true})});}
            var sketch = newSketch(context, id + "F16", { "sketchPlane" : qUnion([Q0])});
            skLineSegment(sketch, "E79", {"start": v(0, 90) * mm, "end": v(0, 120) * mm, "construction": true});
            skCircle(sketch, "E80", {"center": v(0, 120) * mm, "radius": 6 * mm});
            skArc(sketch, "E81", {"start": v(15, 120) * mm, "mid": v(0, 135) * mm, "end": v(-15, 120) * mm});
            skLineSegment(sketch, "E82", {"start": v(-15, 120) * mm, "end": v(-15, 108) * mm});
            skLineSegment(sketch, "E83", {"start": v(-15, 108) * mm, "end": v(-33, 90) * mm});
            skLineSegment(sketch, "E84", {"start": v(15, 120) * mm, "end": v(15, 108) * mm});
            skLineSegment(sketch, "E85", {"start": v(15, 108) * mm, "end": v(33, 90) * mm});
            skLineSegment(sketch, "E86", {"start": v(-80, 0) * mm, "end": v(80, 0) * mm, "construction": true});
            skCircle(sketch, "E87.MirrorC", {"center": v(0, -120) * mm, "radius": 6 * mm});
            skLineSegment(sketch, "E88.MirrorCS", {"start": v(-15, -120) * mm, "end": v(-15, -108) * mm});
            skLineSegment(sketch, "E89.MirrorCS", {"start": v(15, -120) * mm, "end": v(15, -108) * mm});
            skLineSegment(sketch, "E90.MirrorCS", {"start": v(15, -108) * mm, "end": v(33, -90) * mm});
            skLineSegment(sketch, "E91.MirrorCS", {"start": v(-15, -108) * mm, "end": v(-33, -90) * mm});
            skArc(sketch, "E92.MirrorCS", {"start": v(15, -120) * mm, "mid": v(0, -135) * mm, "end": v(-15, -120) * mm});
            skLineSegment(sketch, "E93.MirrorCS", {"start": v(0, -90) * mm, "end": v(0, -120) * mm, "construction": true});
            skSolve(sketch);
        }
        {
            var Q0;
            Q0=makeQuery(id+"F16.imprint","IMPRINT",FACE,{"disambiguationData":[TD([[makeQuery(id+"F16.imprint","IMPRINT",EDGE,{"derivedFrom":makeQuery(id+"F1.opExtrude","CAP_EDGE",EDGE,{"disambiguationData":[OSD([sQuery(id+"F0.wireOp",EDGE,"E1.left")])],"isStart":true})}),-1.0]])]});
            var Q1;
            Q1=makeQuery(id+"F16.imprint","IMPRINT",FACE,{"disambiguationData":[TD([[makeQuery(id+"F16.imprint","IMPRINT",EDGE,{"derivedFrom":sQuery(id+"F16.wireOp",EDGE,"E80")}),-1.0]])]});
            var Q2;
            Q2=makeQuery(id+"F16.imprint","IMPRINT",FACE,{"disambiguationData":[TD([[makeQuery(id+"F16.imprint","IMPRINT",EDGE,{"derivedFrom":sQuery(id+"F16.wireOp",EDGE,"E87.MirrorC")}),1.0]])]});
            var Q3;
            Q3=makeQuery(id+"F2.opExtrude","CAP_FACE",FACE,{"disambiguationData":[OSD([sQuery(id+"F0.wireOp",EDGE,"E12"),sQuery(id+"F0.wireOp",EDGE,"E13"),sQuery(id+"F0.wireOp",EDGE,"E14"),sQuery(id+"F0.wireOp",EDGE,"E15"),sQuery(id+"F0.wireOp",EDGE,"E17.filletArc"),sQuery(id+"F0.wireOp",EDGE,"E18.filletArc"),sQuery(id+"F0.wireOp",EDGE,"E19.filletArc"),sQuery(id+"F0.wireOp",EDGE,"E20.filletArc"),sQuery(id+"F0.wireOp",EDGE,"E25.0"),sQuery(id+"F0.wireOp",EDGE,"E25.1"),sQuery(id+"F0.wireOp",EDGE,"E25.2"),sQuery(id+"F0.wireOp",EDGE,"E25.3"),sQuery(id+"F0.wireOp",EDGE,"E25.4"),sQuery(id+"F0.wireOp",EDGE,"E25.5"),sQuery(id+"F0.wireOp",EDGE,"E25.6"),sQuery(id+"F0.wireOp",EDGE,"E25.7")])],"isStart":false});
            extrude(context, id + "F17", {"entities" : qUnion([Q0, Q1, Q2]), "endBound" : BoundingType.UP_TO_SURFACE, "endBoundEntityFace" : qUnion([Q3]), "depth" : 25 * mm});
        }
    });
